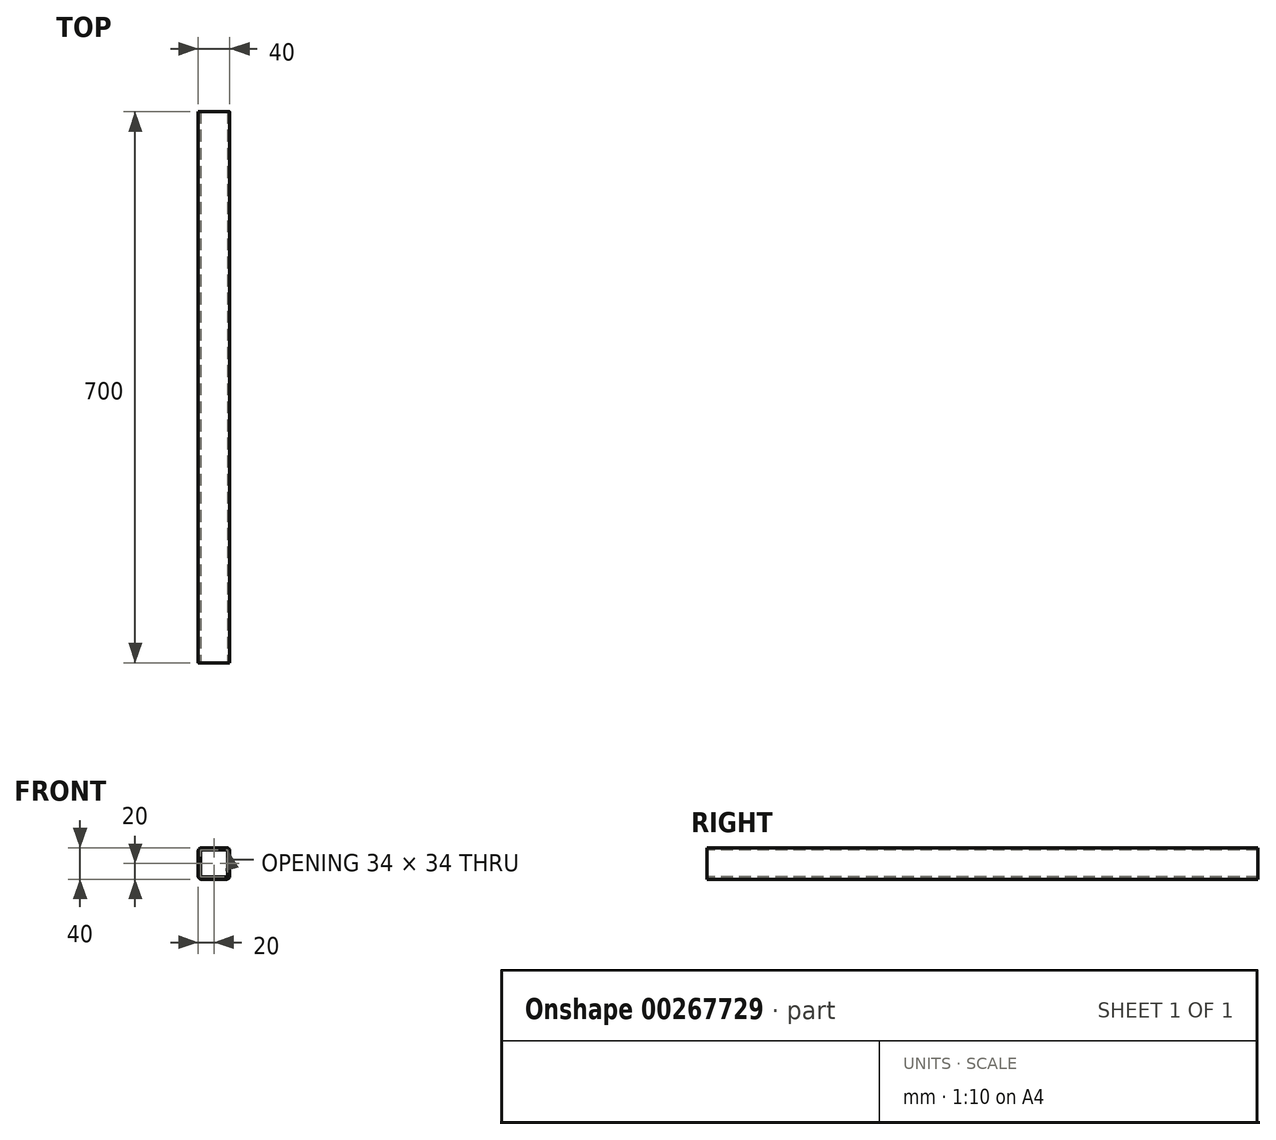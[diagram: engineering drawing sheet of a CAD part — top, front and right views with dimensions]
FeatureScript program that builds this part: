
annotation { "Feature Type Name" : "Feature", "Feature Type Description" : "" }
export const myFeature = defineFeature(function(context is Context, id is Id, definition is map)
    precondition{}
    {
        {
            var Q0;
            Q0=qCreatedBy(makeId("Front.planeOp"),FACE);
            var sketch = newSketch(context, id + "F0", { "sketchPlane" : qUnion([Q0])});
            skLineSegment(sketch, "E0.bottom", {"start": v(16, -20) * mm, "end": v(-16, -20) * mm});
            skLineSegment(sketch, "E0.top", {"start": v(16, 20) * mm, "end": v(-16, 20) * mm});
            skLineSegment(sketch, "E0.left", {"start": v(20, -16) * mm, "end": v(20, 16) * mm});
            skLineSegment(sketch, "E0.right", {"start": v(-20, -16) * mm, "end": v(-20, 16) * mm});
            skPoint(sketch, "E0.middle", {"position": v(0, 0) * mm});
            skPoint(sketch, "E1.visualSharp", {"position": v(-20, 20) * mm});
            skArc(sketch, "E1.filletArc", {"start": v(-16, 20) * mm, "mid": v(-18.83, 18.83) * mm, "end": v(-20, 16) * mm});
            skPoint(sketch, "E2.visualSharp", {"position": v(20, 20) * mm});
            skArc(sketch, "E2.filletArc", {"start": v(20, 16) * mm, "mid": v(18.83, 18.83) * mm, "end": v(16, 20) * mm});
            skPoint(sketch, "E3.visualSharp", {"position": v(20, -20) * mm});
            skArc(sketch, "E3.filletArc", {"start": v(16, -20) * mm, "mid": v(18.83, -18.83) * mm, "end": v(20, -16) * mm});
            skPoint(sketch, "E4.visualSharp", {"position": v(-20, -20) * mm});
            skArc(sketch, "E4.filletArc", {"start": v(-20, -16) * mm, "mid": v(-18.83, -18.83) * mm, "end": v(-16, -20) * mm});
            skArc(sketch, "E5.0", {"start": v(-17, -16) * mm, "mid": v(-16.7, -16.7) * mm, "end": v(-16, -17) * mm});
            skLineSegment(sketch, "E5.1", {"start": v(16, -17) * mm, "end": v(-16, -17) * mm});
            skLineSegment(sketch, "E5.2", {"start": v(-17, -16) * mm, "end": v(-17, 16) * mm});
            skArc(sketch, "E5.3", {"start": v(16, -17) * mm, "mid": v(16.7, -16.7) * mm, "end": v(17, -16) * mm});
            skArc(sketch, "E5.4", {"start": v(-16, 17) * mm, "mid": v(-16.7, 16.7) * mm, "end": v(-17, 16) * mm});
            skLineSegment(sketch, "E5.5", {"start": v(16, 17) * mm, "end": v(-16, 17) * mm});
            skArc(sketch, "E5.6", {"start": v(17, 16) * mm, "mid": v(16.7, 16.7) * mm, "end": v(16, 17) * mm});
            skLineSegment(sketch, "E5.7", {"start": v(17, -16) * mm, "end": v(17, 16) * mm});
            skSolve(sketch);
        }
        {
            var Q0;
            Q0=qSketchRegion(id+"F0",true);
            extrude(context, id + "F1", {"entities" : qUnion([Q0]), "oppositeDirection" : true, "depth" : 700 * mm});
        }
    });
